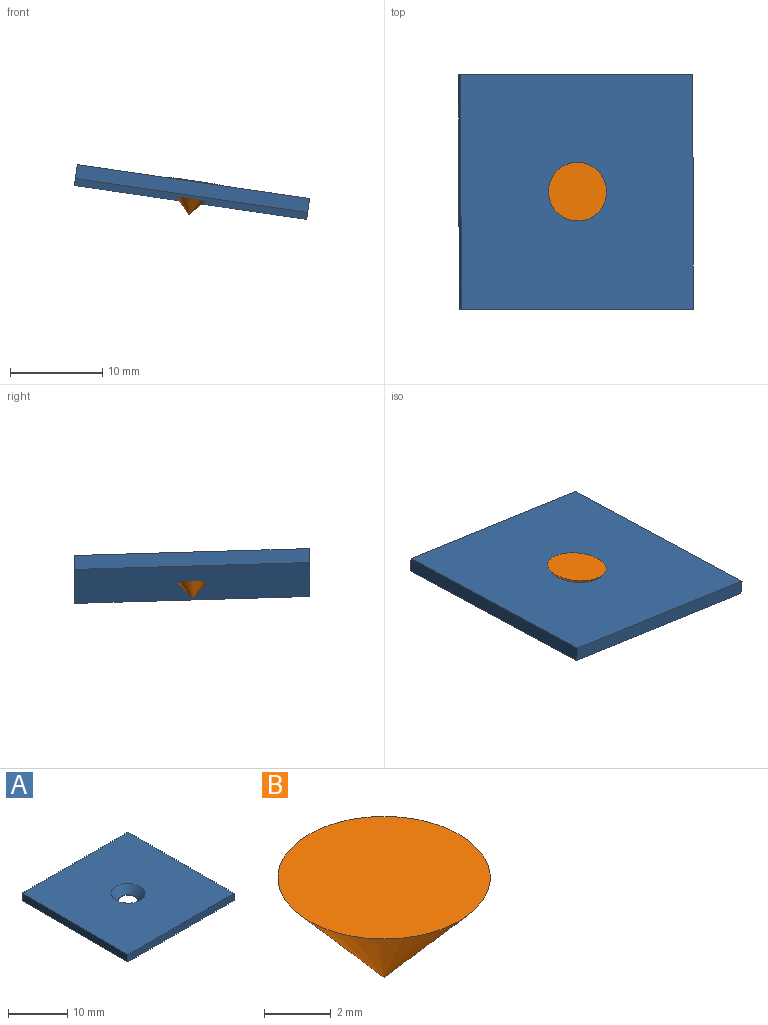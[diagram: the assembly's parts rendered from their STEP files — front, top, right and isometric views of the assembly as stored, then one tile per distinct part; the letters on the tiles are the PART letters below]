
ASSEMBLY  parts=2 mates=1
PART A: 8 faces, bbox 25.4x25.4x1.5 mm
  f0: plane 25.4x1.52mm, normal (0,-1,0), area 38.7mm2, adj f1,f4,f5,f6
  f1: plane 25.4x1.52mm, normal (1,0,0), area 38.7mm2, adj f0,f2,f5,f6
  f2: plane 25.4x1.52mm, normal (0,1,0), area 38.7mm2, adj f1,f4,f5,f6
  f3: cylinder r=1.63mm len=3.25mm, axis (0,0,-1), area 0.8mm2, adj f6,f7
  f4: plane 25.4x1.52mm, normal (-1,0,0), area 38.7mm2, adj f0,f2,f5,f6
  f5: plane 25.4x25.4mm, normal (0,0,1), area 619mm2, adj f0,f1,f2,f4,f7
  f6: plane 25.4x25.4mm, normal (0,0,-1), area 636.9mm2, adj f0,f1,f2,f3,f4
  f7: cone r=1.63mm half-angle=41deg, axis (0,0,1), area 27.2mm2, adj f3,f5
PART B: 2 faces, bbox 6.4x6.4x3.7 mm
  f0: cone r=3.17mm half-angle=41deg, axis (0,0,1), area 48.3mm2, adj f1
  f1: plane 6.35x6.35mm, normal (0,0,1), area 31.7mm2, adj f0
PLACE A rot(axis=(0.06,0.09,0.99),90.4deg) t=(2.59,12,17.36)mm
PLACE B rot(axis=(-0.2,0.98,0.01),8.5deg) t=(2.34,11.95,15.62)mm
MATE fastened A.f3 <-> B.f0  axis (0.14,0.03,0.99) through (2.61,12,17.43)mm
